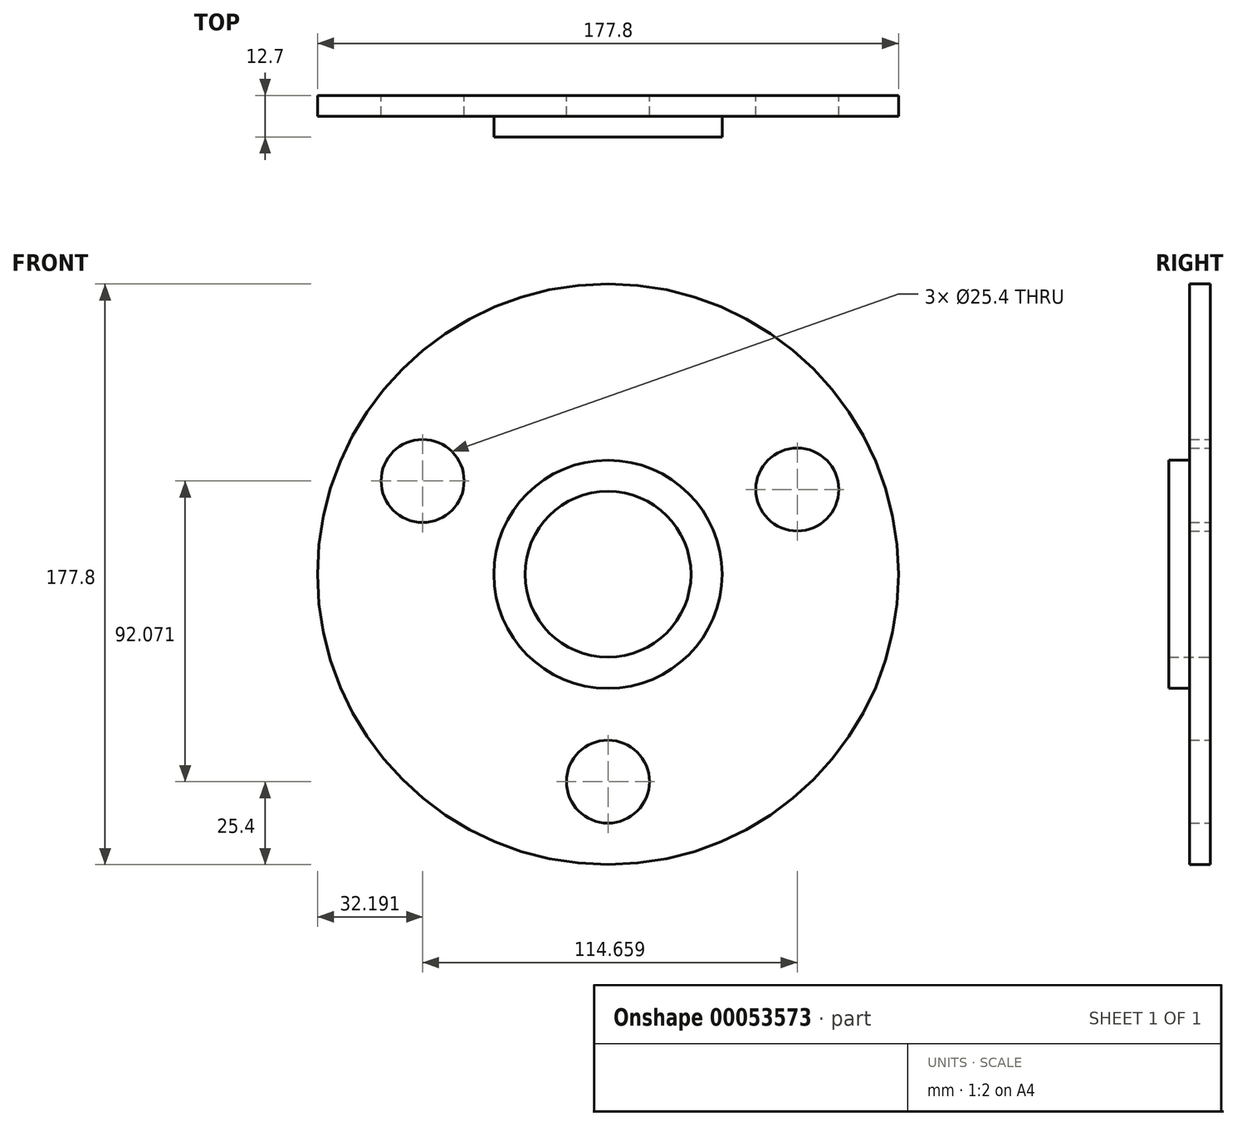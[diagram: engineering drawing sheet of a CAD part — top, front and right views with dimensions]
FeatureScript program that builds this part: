
annotation { "Feature Type Name" : "Feature", "Feature Type Description" : "" }
export const myFeature = defineFeature(function(context is Context, id is Id, definition is map)
    precondition{}
    {
        {
            var Q0;
            Q0=qCreatedBy(makeId("Front.planeOp"),FACE);
            var sketch = newSketch(context, id + "F0", { "sketchPlane" : qUnion([Q0])});
            skCircle(sketch, "E0", {"center": v(0, 0) * mm, "radius": 88.9 * mm});
            skCircle(sketch, "E1", {"center": v(0, 0) * mm, "radius": 34.93 * mm});
            skCircle(sketch, "E2", {"center": v(0, 0) * mm, "radius": 25.4 * mm});
            skCircle(sketch, "E3", {"center": v(0, 0) * mm, "radius": 63.5 * mm, "construction": true});
            skLineSegment(sketch, "E4", {"start": v(0, 0) * mm, "end": v(-9.37, 0) * mm});
            skLineSegment(sketch, "E5", {"start": v(-9.37, 0) * mm, "end": v(9.25, 0) * mm});
            skLineSegment(sketch, "E6", {"start": v(9.25, 0) * mm, "end": v(0, 0) * mm});
            skLineSegment(sketch, "E7", {"start": v(0, 0) * mm, "end": v(0, 10.42) * mm});
            skLineSegment(sketch, "E8", {"start": v(0, 10.42) * mm, "end": v(0, -9.66) * mm});
            skLineSegment(sketch, "E9", {"start": v(20.2, 0) * mm, "end": v(95.06, 0) * mm, "construction": true});
            skLineSegment(sketch, "E10", {"start": v(0, 21.74) * mm, "end": v(0, 98.9) * mm});
            skPoint(sketch, "E10.startSnap0", {"position": v(0, 5.21) * mm});
            skLineSegment(sketch, "E11", {"start": v(-19.52, 0) * mm, "end": v(-97.22, 0) * mm, "construction": true});
            skLineSegment(sketch, "E12", {"start": v(0, -21.46) * mm, "end": v(0, -97.8) * mm, "construction": true});
            skLineSegment(sketch, "E13", {"start": v(-32.46, 12.9) * mm, "end": v(-112.04, 64.32) * mm, "construction": true});
            skLineSegment(sketch, "E14", {"start": v(32.46, 12.9) * mm, "end": v(114.6, 54.99) * mm, "construction": true});
            skCircle(sketch, "E15", {"center": v(57.95, 25.96) * mm, "radius": 12.7 * mm});
            skCircle(sketch, "E16", {"center": v(-56.7, 28.57) * mm, "radius": 12.7 * mm});
            skCircle(sketch, "E17", {"center": v(0, -63.5) * mm, "radius": 12.7 * mm});
            skSolve(sketch);
        }
        {
            var Q0;
            Q0=makeQuery(id+"F0.imprint","IMPRINT",FACE,{"disambiguationData":[TD([[makeQuery(id+"F0.imprint","IMPRINT",EDGE,{"derivedFrom":sQuery(id+"F0.wireOp",EDGE,"E0")}),1.0]])]});
            extrude(context, id + "F1", {"entities" : qUnion([Q0]), "depth" : 6.35 * mm});
        }
        {
            var Q0;
            Q0=makeQuery(id+"F0.imprint","IMPRINT",FACE,{"disambiguationData":[TD([[makeQuery(id+"F0.imprint","IMPRINT",EDGE,{"derivedFrom":sQuery(id+"F0.wireOp",EDGE,"E1")}),1.0]])]});
            extrude(context, id + "F2", {"entities" : qUnion([Q0]), "operationType" : NewBodyOperationType.ADD, "depth" : 12.7 * mm});
        }
    });
